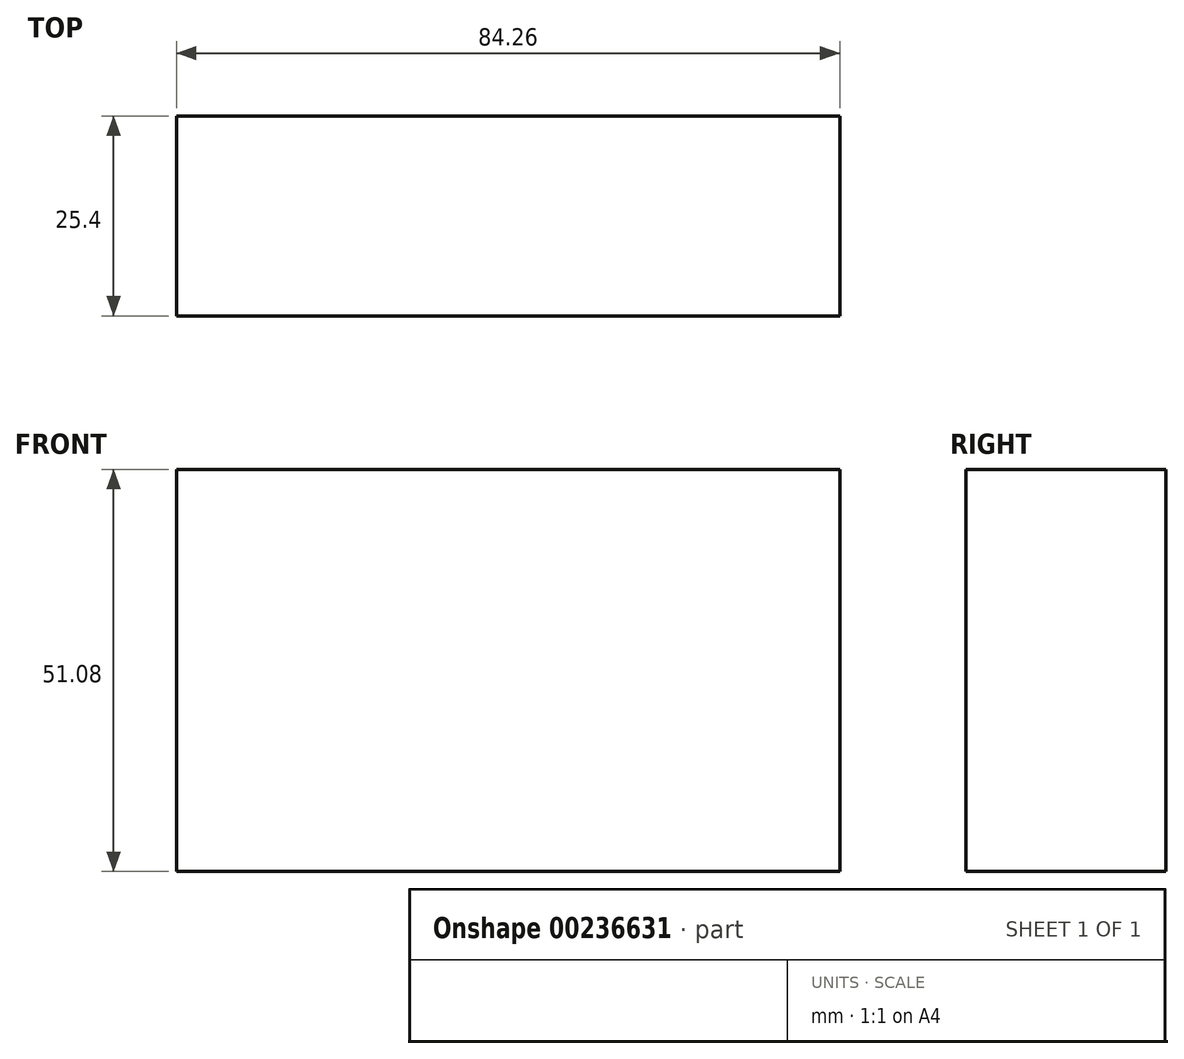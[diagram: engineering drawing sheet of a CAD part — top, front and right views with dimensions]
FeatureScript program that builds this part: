
annotation { "Feature Type Name" : "Feature", "Feature Type Description" : "" }
export const myFeature = defineFeature(function(context is Context, id is Id, definition is map)
    precondition{}
    {
        {
            var Q0;
            Q0=qCreatedBy(makeId("Front.planeOp"),FACE);
            var sketch = newSketch(context, id + "F0", { "sketchPlane" : qUnion([Q0])});
            skLineSegment(sketch, "E0.bottom", {"start": v(-140.98, -13.65) * mm, "end": v(-56.72, -13.65) * mm});
            skLineSegment(sketch, "E0.top", {"start": v(-140.98, -64.73) * mm, "end": v(-56.72, -64.73) * mm});
            skLineSegment(sketch, "E0.left", {"start": v(-140.98, -13.65) * mm, "end": v(-140.98, -64.73) * mm});
            skLineSegment(sketch, "E0.right", {"start": v(-56.72, -13.65) * mm, "end": v(-56.72, -64.73) * mm});
            skSolve(sketch);
        }
        {
            var Q0;
            Q0 = qSketchRegion(id + "F0", true);
            extrude(context, id + "F1", {"entities" : qUnion([Q0]), "depth" : 25.4 * mm});
        }
    });
